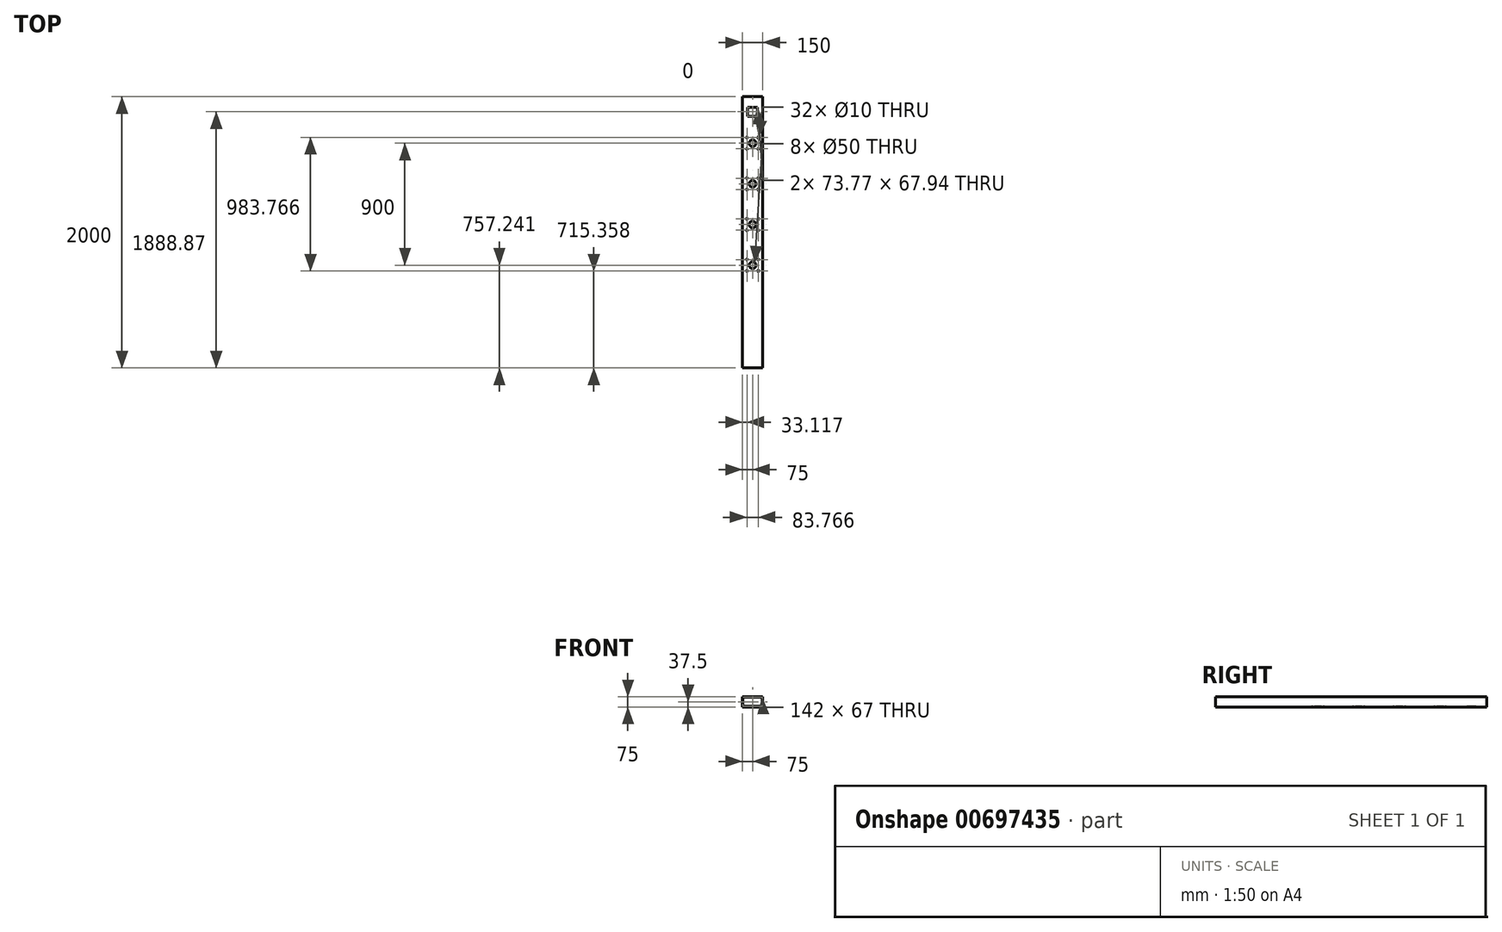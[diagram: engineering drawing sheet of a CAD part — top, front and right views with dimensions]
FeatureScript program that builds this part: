
annotation { "Feature Type Name" : "Feature", "Feature Type Description" : "" }
export const myFeature = defineFeature(function(context is Context, id is Id, definition is map)
    precondition{}
    {
        {
            var Q0;
            Q0=qCreatedBy(makeId("Front.planeOp"),FACE);
            var sketch = newSketch(context, id + "F0", { "sketchPlane" : qUnion([Q0])});
            skLineSegment(sketch, "E0.bottom", {"start": v(-71, 33.5) * mm, "end": v(71, 33.5) * mm});
            skLineSegment(sketch, "E0.top", {"start": v(-71, -33.5) * mm, "end": v(71, -33.5) * mm});
            skLineSegment(sketch, "E0.left", {"start": v(-71, 33.5) * mm, "end": v(-71, -33.5) * mm});
            skLineSegment(sketch, "E0.right", {"start": v(71, 33.5) * mm, "end": v(71, -33.5) * mm});
            skPoint(sketch, "E0.middle", {"position": v(0, 0) * mm});
            skLineSegment(sketch, "E1.bottom", {"start": v(-75, 37.5) * mm, "end": v(75, 37.5) * mm});
            skLineSegment(sketch, "E1.top", {"start": v(-75, -37.5) * mm, "end": v(75, -37.5) * mm});
            skLineSegment(sketch, "E1.left", {"start": v(-75, 37.5) * mm, "end": v(-75, -37.5) * mm});
            skLineSegment(sketch, "E1.right", {"start": v(75, 37.5) * mm, "end": v(75, -37.5) * mm});
            skSolve(sketch);
        }
        {
            var Q0;
            Q0 = qSketchRegion(id + "F0", true);
            extrude(context, id + "F1", {"entities" : qUnion([Q0]), "depth" : 2000 * mm, "offsetDistance" : 25 * mm});
        }
        {
            var Q0;
            Q0=makeQuery(id+"F1.opExtrude","SWEPT_FACE",FACE,{"disambiguationData":[OSD([sQuery(id+"F0.wireOp",EDGE,"E1.bottom")])]});
            var sketch = newSketch(context, id + "F2", { "sketchPlane" : qUnion([Q0])});
            skLineSegment(sketch, "E2.bottom", {"start": v(-36.88, -77.16) * mm, "end": v(36.88, -77.16) * mm});
            skLineSegment(sketch, "E2.top", {"start": v(-36.88, -145.1) * mm, "end": v(36.88, -145.1) * mm});
            skLineSegment(sketch, "E2.left", {"start": v(-36.88, -77.16) * mm, "end": v(-36.88, -145.1) * mm});
            skLineSegment(sketch, "E2.right", {"start": v(36.88, -77.16) * mm, "end": v(36.88, -145.1) * mm});
            skPoint(sketch, "E2.middle", {"position": v(0, -111.13) * mm});
            skCircle(sketch, "E3", {"center": v(0, -342.76) * mm, "radius": 25 * mm});
            skLineSegment(sketch, "E4.bottom", {"start": v(-41.88, -300.88) * mm, "end": v(41.88, -300.88) * mm, "construction": true});
            skLineSegment(sketch, "E4.top", {"start": v(-41.88, -384.64) * mm, "end": v(41.88, -384.64) * mm, "construction": true});
            skLineSegment(sketch, "E4.left", {"start": v(-41.88, -300.88) * mm, "end": v(-41.88, -384.64) * mm, "construction": true});
            skLineSegment(sketch, "E4.right", {"start": v(41.88, -300.88) * mm, "end": v(41.88, -384.64) * mm, "construction": true});
            skCircle(sketch, "E5", {"center": v(-41.88, -300.88) * mm, "radius": 5 * mm});
            skCircle(sketch, "E6", {"center": v(41.88, -300.88) * mm, "radius": 5 * mm});
            skCircle(sketch, "E7", {"center": v(41.88, -384.64) * mm, "radius": 5 * mm});
            skCircle(sketch, "E8", {"center": v(-41.88, -384.64) * mm, "radius": 5 * mm});
            skCircle(sketch, "E9.0.1.0", {"center": v(-41.88, -684.64) * mm, "radius": 5 * mm});
            skCircle(sketch, "E9.0.1.1", {"center": v(41.88, -684.64) * mm, "radius": 5 * mm});
            skCircle(sketch, "E9.0.1.2", {"center": v(41.88, -600.88) * mm, "radius": 5 * mm});
            skCircle(sketch, "E9.0.1.3", {"center": v(-41.88, -600.88) * mm, "radius": 5 * mm});
            skLineSegment(sketch, "E9.0.1.4", {"start": v(-41.88, -684.64) * mm, "end": v(41.88, -684.64) * mm, "construction": true});
            skCircle(sketch, "E9.0.1.5", {"center": v(0, -642.76) * mm, "radius": 25 * mm});
            skPoint(sketch, "E9.0.1.6", {"position": v(0, -642.76) * mm});
            skLineSegment(sketch, "E9.0.1.7", {"start": v(-41.88, -600.88) * mm, "end": v(-41.88, -684.64) * mm, "construction": true});
            skLineSegment(sketch, "E9.0.1.8", {"start": v(-41.88, -600.88) * mm, "end": v(41.88, -600.88) * mm, "construction": true});
            skLineSegment(sketch, "E9.0.1.9", {"start": v(41.88, -600.88) * mm, "end": v(41.88, -684.64) * mm, "construction": true});
            skCircle(sketch, "E9.0.2.0", {"center": v(-41.88, -984.64) * mm, "radius": 5 * mm});
            skCircle(sketch, "E9.0.2.1", {"center": v(41.88, -984.64) * mm, "radius": 5 * mm});
            skCircle(sketch, "E9.0.2.2", {"center": v(41.88, -900.88) * mm, "radius": 5 * mm});
            skCircle(sketch, "E9.0.2.3", {"center": v(-41.88, -900.88) * mm, "radius": 5 * mm});
            skLineSegment(sketch, "E9.0.2.4", {"start": v(-41.88, -984.64) * mm, "end": v(41.88, -984.64) * mm, "construction": true});
            skCircle(sketch, "E9.0.2.5", {"center": v(0, -942.76) * mm, "radius": 25 * mm});
            skPoint(sketch, "E9.0.2.6", {"position": v(0, -942.76) * mm});
            skLineSegment(sketch, "E9.0.2.7", {"start": v(-41.88, -900.88) * mm, "end": v(-41.88, -984.64) * mm, "construction": true});
            skLineSegment(sketch, "E9.0.2.8", {"start": v(-41.88, -900.88) * mm, "end": v(41.88, -900.88) * mm, "construction": true});
            skLineSegment(sketch, "E9.0.2.9", {"start": v(41.88, -900.88) * mm, "end": v(41.88, -984.64) * mm, "construction": true});
            skCircle(sketch, "E9.0.3.0", {"center": v(-41.88, -1284.64) * mm, "radius": 5 * mm});
            skCircle(sketch, "E9.0.3.1", {"center": v(41.88, -1284.64) * mm, "radius": 5 * mm});
            skCircle(sketch, "E9.0.3.2", {"center": v(41.88, -1200.88) * mm, "radius": 5 * mm});
            skCircle(sketch, "E9.0.3.3", {"center": v(-41.88, -1200.88) * mm, "radius": 5 * mm});
            skLineSegment(sketch, "E9.0.3.4", {"start": v(-41.88, -1284.64) * mm, "end": v(41.88, -1284.64) * mm, "construction": true});
            skCircle(sketch, "E9.0.3.5", {"center": v(0, -1242.76) * mm, "radius": 25 * mm});
            skPoint(sketch, "E9.0.3.6", {"position": v(0, -1242.76) * mm});
            skLineSegment(sketch, "E9.0.3.7", {"start": v(-41.88, -1200.88) * mm, "end": v(-41.88, -1284.64) * mm, "construction": true});
            skLineSegment(sketch, "E9.0.3.8", {"start": v(-41.88, -1200.88) * mm, "end": v(41.88, -1200.88) * mm, "construction": true});
            skLineSegment(sketch, "E9.0.3.9", {"start": v(41.88, -1200.88) * mm, "end": v(41.88, -1284.64) * mm, "construction": true});
            skLineSegment(sketch, "E9.direction1", {"start": v(-41.88, -384.64) * mm, "end": v(-7.5, -384.64) * mm, "construction": true});
            skLineSegment(sketch, "E9.direction2", {"start": v(-41.88, -384.64) * mm, "end": v(-41.88, -684.64) * mm, "construction": true});
            skSolve(sketch);
        }
        {
            var Q0;
            Q0 = qSketchRegion(id + "F2", true);
            extrude(context, id + "F3", {"entities" : qUnion([Q0]), "operationType" : NewBodyOperationType.REMOVE, "endBound" : BoundingType.THROUGH_ALL, "oppositeDirection" : true, "depth" : 25 * mm, "offsetDistance" : 25 * mm});
        }
    });
